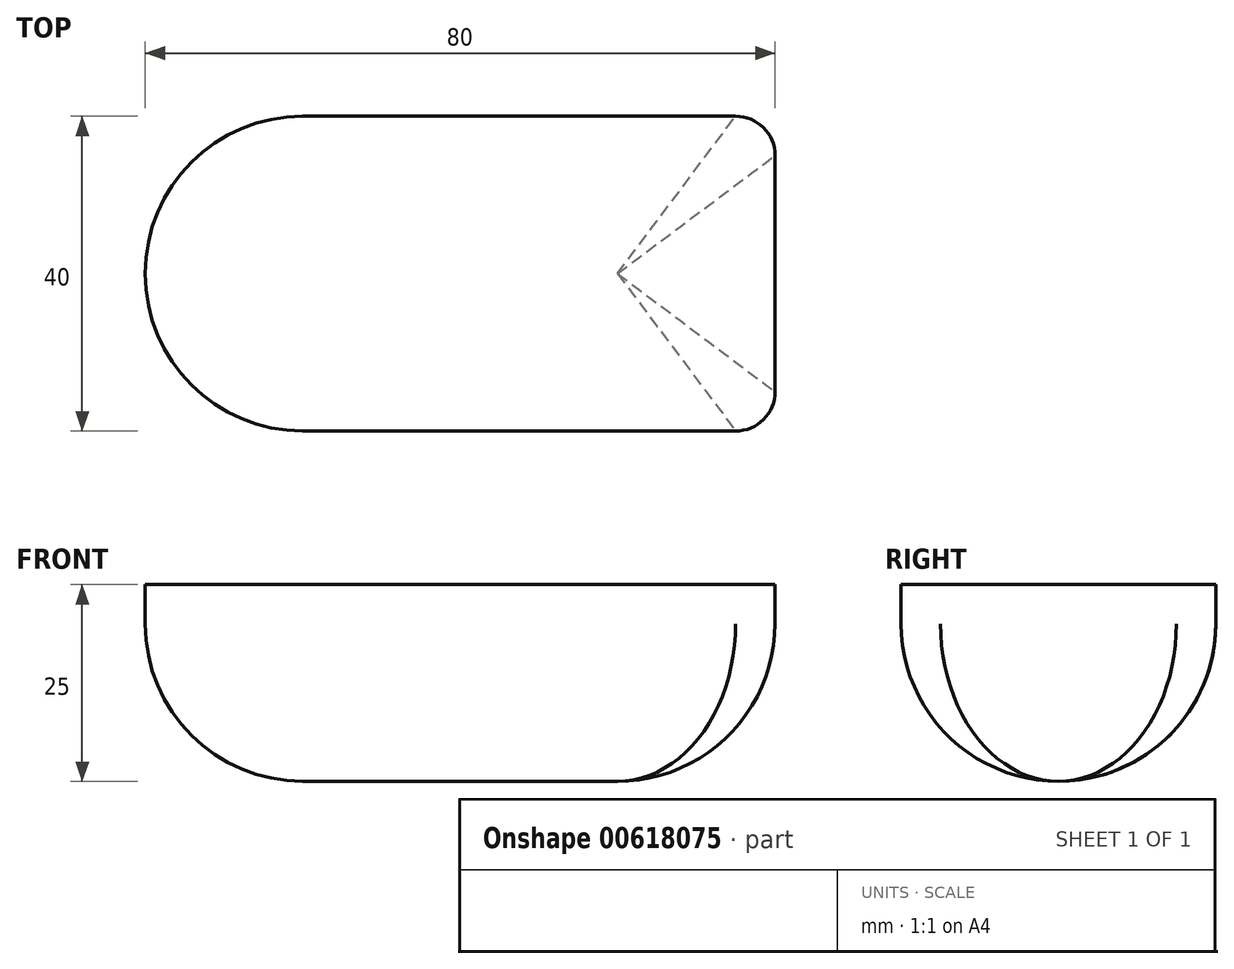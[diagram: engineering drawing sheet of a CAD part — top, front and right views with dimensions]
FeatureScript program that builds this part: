
annotation { "Feature Type Name" : "Feature", "Feature Type Description" : "" }
export const myFeature = defineFeature(function(context is Context, id is Id, definition is map)
    precondition{}
    {
        {
            var Q0;
            Q0=qCreatedBy(makeId("Top.planeOp"),FACE);
            var sketch = newSketch(context, id + "F0", { "sketchPlane" : qUnion([Q0])});
            skLineSegment(sketch, "E0.bottom", {"start": v(0, 0) * mm, "end": v(80, 0) * mm});
            skLineSegment(sketch, "E0.top", {"start": v(0, 40) * mm, "end": v(80, 40) * mm});
            skLineSegment(sketch, "E0.left", {"start": v(0, 0) * mm, "end": v(0, 40) * mm});
            skLineSegment(sketch, "E0.right", {"start": v(80, 0) * mm, "end": v(80, 40) * mm});
            skSolve(sketch);
        }
        {
            var Q0;
            Q0 = qSketchRegion(id + "F0", true);
            extrude(context, id + "F1", {"entities" : qUnion([Q0]), "depth" : 25 * mm, "offsetDistance" : 25 * mm});
        }
        {
            var Q0;
            Q0=makeQuery(id+"F1.opExtrude","SWEPT_EDGE",EDGE,{"disambiguationData":[OSD([sQuery(id+"F0.wireOp",EDGE,"E0.top"),sQuery(id+"F0.wireOp",EDGE,"E0.left")])]});
            var Q1;
            Q1=makeQuery(id+"F1.opExtrude","SWEPT_EDGE",EDGE,{"disambiguationData":[OSD([sQuery(id+"F0.wireOp",EDGE,"E0.bottom"),sQuery(id+"F0.wireOp",EDGE,"E0.left")])]});
            fillet(context, id + "F2", {"entities" : qUnion([Q0, Q1]), "radius" : 20 * mm, "tangentPropagation" : true, "allowEdgeOverflow" : false});
        }
        {
            var Q0;
            Q0=makeQuery(id+"F1.opExtrude","SWEPT_EDGE",EDGE,{"disambiguationData":[OSD([sQuery(id+"F0.wireOp",EDGE,"E0.top"),sQuery(id+"F0.wireOp",EDGE,"E0.right")])]});
            var Q1;
            Q1=makeQuery(id+"F1.opExtrude","SWEPT_EDGE",EDGE,{"disambiguationData":[OSD([sQuery(id+"F0.wireOp",EDGE,"E0.bottom"),sQuery(id+"F0.wireOp",EDGE,"E0.right")])]});
            fillet(context, id + "F3", {"entities" : qUnion([Q0, Q1]), "radius" : 5 * mm, "tangentPropagation" : true, "allowEdgeOverflow" : false});
        }
        {
            var Q0;
            Q0=makeQuery(id+"F1.opExtrude","CAP_FACE",FACE,{"disambiguationData":[OSD([sQuery(id+"F0.wireOp",EDGE,"E0.bottom"),sQuery(id+"F0.wireOp",EDGE,"E0.top"),sQuery(id+"F0.wireOp",EDGE,"E0.left"),sQuery(id+"F0.wireOp",EDGE,"E0.right")])],"isStart":true});
            fillet(context, id + "F4", {"entities" : qUnion([Q0]), "radius" : 20 * mm, "tangentPropagation" : true, "allowEdgeOverflow" : false});
        }
    });
